# Revit family: STH20963PTO_27
name_source: partatom
category: Luminárias
units: mm (PartAtom-declared; Revit-internal decimal feet)

## family parameters
Compartilhado = Não
Corte com vazios quando carregada = Não
Cota do conector redondo = Utilizar diâmetro
Fonte luminosa = Sim
Hospedeiro = Forro
Manter orientação da anotação = Não
Número OmniClass = 23.80.70.11
Ponto de cálculo do ambiente = Não
Sempre na vertical = Sim
Tipo de parte = Normal
Título OmniClass = Luminaries for Internal Lighting

## types (1)
- STH20963PTO/27 - PRETO - 1m - 2700K - 350lm - 90°
    Altura = 0.03 m
    Arquivo de rede fotométrica = STELLA - STH20963PTO-27 - ARCHI - PERFIL DE SOBREPOR PLANO.ies
    Comprimento = 1.01 m
    Dimerização = Não dimerizável
    Elevação padrão = 0 m
    Estrutura = Al - Preto
    Fabricante = Stella
    Filtro de cor = 16777215
    Fluxo Luminoso = 350 lm
    Grau de proteção (IP) = IP20
    IRC (Índice de reprodução de cores) = >93 (R9 >60)
    Largura = 0.03 m
    Luminoso = Luminoso_Lente Preta - 2700K
    Modelo = Archi
    Potência = 19 W
    Referência = STH20963PTO/27 - PRETO - 1m
    Temperatura da cor (K) = 2700 K
    Tensão Elétrica = 24V
    Troca de temperatura da cor de lâmpada com esmaecimento = <Nenhum>
    URL = https://stella.com.br
    Ângulo de Abertura = 90°
    Ângulo de inclinação = 90.00°
